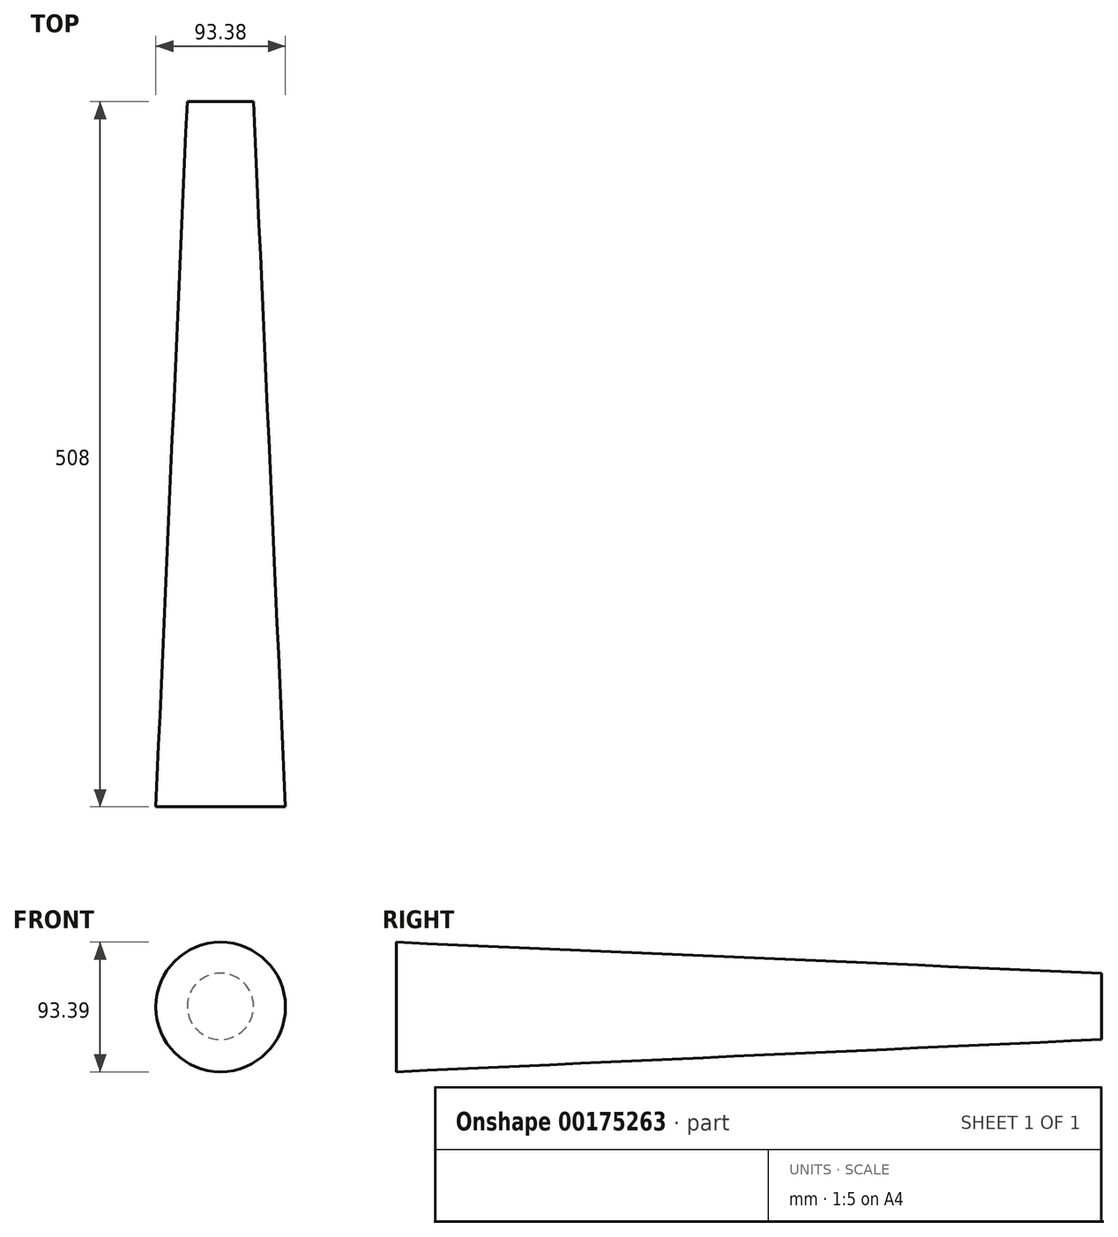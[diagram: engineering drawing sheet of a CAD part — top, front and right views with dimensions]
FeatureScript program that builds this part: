
annotation { "Feature Type Name" : "Feature", "Feature Type Description" : "" }
export const myFeature = defineFeature(function(context is Context, id is Id, definition is map)
    precondition{}
    {
        {
            var Q0;
            Q0=qCreatedBy(makeId("Front.planeOp"),FACE);
            var sketch = newSketch(context, id + "F0", { "sketchPlane" : qUnion([Q0])});
            skCircle(sketch, "E0", {"center": v(-19.37, 20.41) * mm, "radius": 23.87 * mm});
            skSolve(sketch);
        }
        {
            var Q0;
            Q0=qCreatedBy(makeId("Front.planeOp"),FACE);
            cPlane(context, id + "F1", {"entities" : qUnion([Q0]), "cplaneType" : CPlaneType.OFFSET, "offset" : 508 * mm, "width" : 152.4 * mm, "height" : 152.4 * mm});
        }
        {
            var Q0;
            Q0=qCreatedBy(id+"F1.planeOp",FACE);
            var sketch = newSketch(context, id + "F2", { "sketchPlane" : qUnion([Q0])});
            skCircle(sketch, "E1", {"center": v(-19.2, 19.92) * mm, "radius": 46.7 * mm});
            skSolve(sketch);
        }
        {
            var Q0;
            Q0=makeQuery(id+"F0.imprint","IMPRINT",FACE,{"disambiguationData":[TD([[makeQuery(id+"F0.imprint","IMPRINT",EDGE,{"derivedFrom":sQuery(id+"F0.wireOp",EDGE,"E0")}),1.0]])]});
            var Q1;
            Q1=makeQuery(id+"F2.imprint","IMPRINT",FACE,{"disambiguationData":[TD([[makeQuery(id+"F2.imprint","IMPRINT",EDGE,{"derivedFrom":sQuery(id+"F2.wireOp",EDGE,"E1")}),1.0]])]});
            loft(context, id + "F3", {"sheetProfilesArray" : [{ "sheetProfileEntities" : qUnion([Q0]) }, { "sheetProfileEntities" : qUnion([Q1]) }]});
        }
    });
